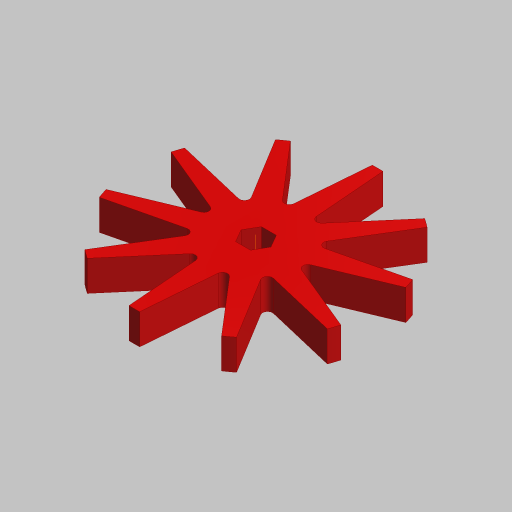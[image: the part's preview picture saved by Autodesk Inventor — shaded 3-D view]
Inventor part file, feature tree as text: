
AUTODESK INVENTOR PART (.ipt)
format: ipt  version: 2023.5 (Build 275446000, 446)  size: 141,312 bytes
history: native  units: mm (DEFAULTED — no unit token found)
features: extrude x1, sketch x1, other x1
ambient origin geometry x8: Origin, YZ Plane, XZ Plane, XY Plane, X Axis, Y Axis, Z Axis, Center Point
bodies: Solid1 (feature_tree)
feature tree (3):
  extrude  "Extrusion1"  TaperAngle=0.0deg  [1 undecoded]
  sketch  "Sketch1"  dims[d0=101.6mm d1=0.0mm d2=0.0mm]
  other  "Cut-Extrude1"
note: 1 required parameter value undecoded (feature->parameter linkage not recoverable at this tier; creation-order binding heuristic only, values carry confidence <= 0.55)
